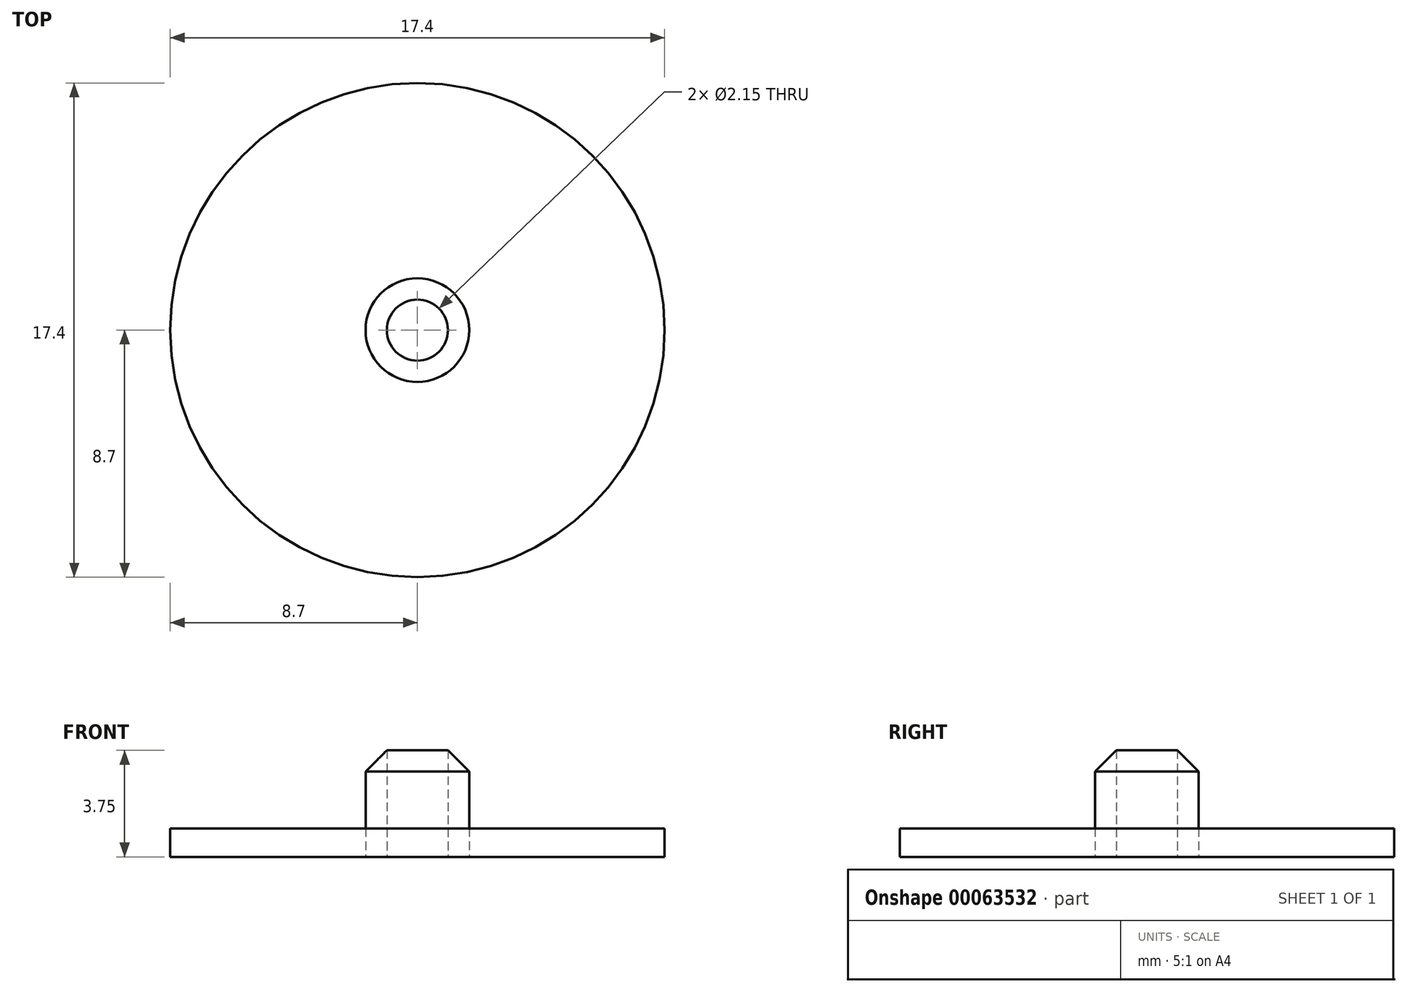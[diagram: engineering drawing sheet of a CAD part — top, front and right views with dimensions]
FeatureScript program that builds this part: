
annotation { "Feature Type Name" : "Feature", "Feature Type Description" : "" }
export const myFeature = defineFeature(function(context is Context, id is Id, definition is map)
    precondition{}
    {
        {
            var Q0;
            Q0=qCreatedBy(makeId("Top.planeOp"),FACE);
            var sketch = newSketch(context, id + "F4", { "sketchPlane" : qUnion([Q0])});
            skCircle(sketch, "E0", {"center": v(0, 0) * mm, "radius": 8.7 * mm});
            skSolve(sketch);
        }
        {
            var Q0;
            Q0=qSketchRegion(id+"F4",true);
            extrude(context, id + "F0", {"entities" : qUnion([Q0]), "depth" : 1 * mm});
        }
        {
            var Q0;
            Q0=qCreatedBy(makeId("Top.planeOp"),FACE);
            var sketch = newSketch(context, id + "F5", { "sketchPlane" : qUnion([Q0])});
            skCircle(sketch, "E1", {"center": v(0, 0) * mm, "radius": 1.82 * mm});
            skSolve(sketch);
        }
        {
            var Q0;
            Q0=qSketchRegion(id+"F5",true);
            extrude(context, id + "F1", {"entities" : qUnion([Q0]), "depth" : (1 + 3) * mm});
        }
        {
            var Q0;
            Q0=sQuery(id+"F5.wireOp",VERTEX,"E1.center");
            var Q1;
            Q1=makeQuery(id+"F0.opExtrude","SWEPT_BODY",BODY,{"disambiguationData":[OSD([sQuery(id+"F4.wireOp",EDGE,"E0")])]});
            var Q2;
            Q2=makeQuery(id+"F1.opExtrude","SWEPT_BODY",BODY,{"disambiguationData":[OSD([sQuery(id+"F5.wireOp",EDGE,"E1")])]});
            hole(context, id + "F2", {"style" : HoleStyle.SIMPLE, "holeDiameter" : (1.75 + .4) * mm, "endStyle" : HoleEndStyle.THROUGH, "oppositeDirection" : true, "locations" : qUnion([Q0]), "scope" : qUnion([Q1, Q2])});
        }
        {
            var Q0;
            Q0=makeQuery(id+"F1.opExtrude","CAP_EDGE",EDGE,{"disambiguationData":[OSD([sQuery(id+"F5.wireOp",EDGE,"E1")])],"isStart":false});
            var Q1;
            Q1=makeQuery(id+"F2.hole-0.boolean.opBoolean","COPY",EDGE,{"disambiguationData":[OD(0.0)],"derivedFrom":makeQuery(id+"F2.hole-0.opRevolve","SWEPT_EDGE",EDGE,{"disambiguationData":[OSD([sQuery(id+"F2.hole-0.sketch.wireOp",EDGE,"core_line_2"),sQuery(id+"F2.hole-0.sketch.wireOp",EDGE,"core_line_3")])]})});
            chamfer(context, id + "F3", {"entities" : qUnion([Q0, Q1]), "width" : 1 * mm});
        }
    });
